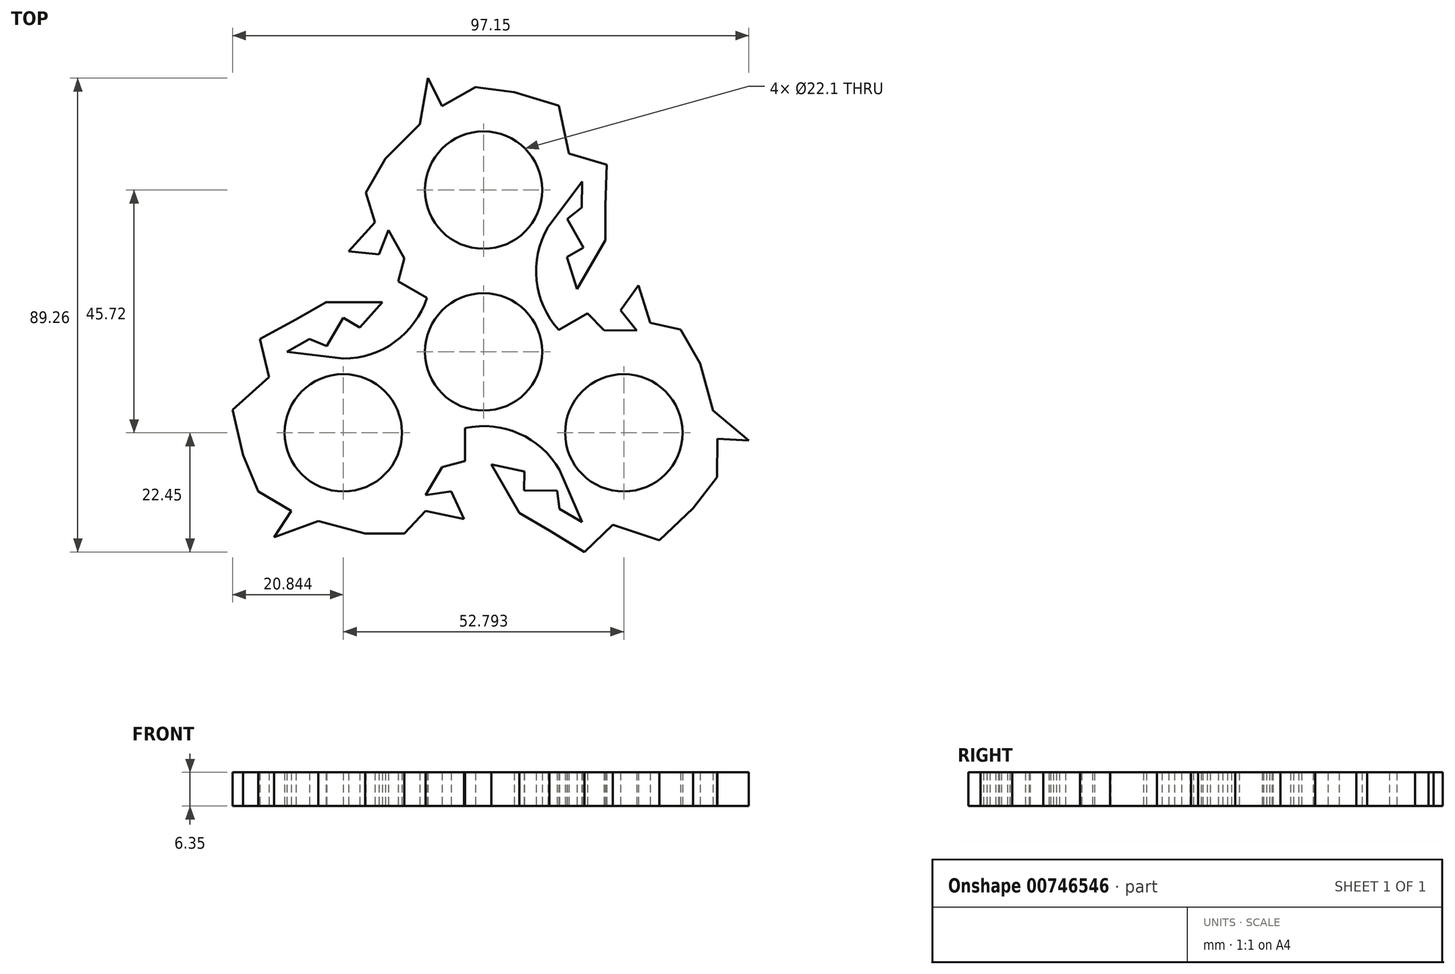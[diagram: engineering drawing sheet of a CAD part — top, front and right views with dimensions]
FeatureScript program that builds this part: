
annotation { "Feature Type Name" : "Feature", "Feature Type Description" : "" }
export const myFeature = defineFeature(function(context is Context, id is Id, definition is map)
    precondition{}
    {
        {
            var Q0;
            Q0=qCreatedBy(makeId("Top.planeOp"),FACE);
            var sketch = newSketch(context, id + "F0", { "sketchPlane" : qUnion([Q0])});
            skCircle(sketch, "E0", {"center": v(0, 0) * mm, "radius": 11.05 * mm});
            skCircle(sketch, "E1", {"center": v(0, 0) * mm, "radius": 13.97 * mm});
            skCircle(sketch, "E2", {"center": v(0, 30.48) * mm, "radius": 11.05 * mm});
            skCircle(sketch, "E3", {"center": v(0, 30.48) * mm, "radius": 13.97 * mm});
            skCircle(sketch, "E4.1.0", {"center": v(-26.4, -15.24) * mm, "radius": 13.97 * mm});
            skCircle(sketch, "E4.1.1", {"center": v(-26.4, -15.24) * mm, "radius": 11.05 * mm});
            skCircle(sketch, "E4.2.0", {"center": v(26.4, -15.24) * mm, "radius": 13.97 * mm});
            skCircle(sketch, "E4.2.1", {"center": v(26.4, -15.24) * mm, "radius": 11.05 * mm});
            skArc(sketch, "E5", {"start": v(-26.4, -1.27) * mm, "mid": v(-12.1, 6.99) * mm, "end": v(-12.1, 23.5) * mm});
            skArc(sketch, "E6.1.0", {"start": v(14.3, -22.22) * mm, "mid": v(0, -13.97) * mm, "end": v(-14.3, -22.23) * mm});
            skArc(sketch, "E6.2.0", {"start": v(12.1, 23.5) * mm, "mid": v(12.1, 6.99) * mm, "end": v(26.4, -1.27) * mm});
            skLineSegment(sketch, "E7", {"start": v(-37.03, 0) * mm, "end": v(-32.77, 2.41) * mm});
            skLineSegment(sketch, "E8", {"start": v(-32.77, 2.41) * mm, "end": v(-29.55, 1.1) * mm});
            skLineSegment(sketch, "E9", {"start": v(-29.55, 1.1) * mm, "end": v(-26.4, 6.44) * mm});
            skLineSegment(sketch, "E10", {"start": v(-26.4, 6.44) * mm, "end": v(-23.32, 4.62) * mm});
            skLineSegment(sketch, "E11", {"start": v(-23.32, 4.62) * mm, "end": v(-19.05, 9.33) * mm});
            skLineSegment(sketch, "E12", {"start": v(-19.05, 9.33) * mm, "end": v(-23.12, 9.33) * mm});
            skLineSegment(sketch, "E13", {"start": v(-23.12, 9.33) * mm, "end": v(-29.65, 9.33) * mm});
            skLineSegment(sketch, "E14", {"start": v(-29.65, 9.33) * mm, "end": v(-35.32, 6.1) * mm});
            skLineSegment(sketch, "E15", {"start": v(-35.32, 6.1) * mm, "end": v(-42.13, 2.41) * mm});
            skLineSegment(sketch, "E16", {"start": v(-42.13, 2.41) * mm, "end": v(-40.37, -4.74) * mm});
            skLineSegment(sketch, "E17", {"start": v(-40.37, -4.74) * mm, "end": v(-47.24, -10.92) * mm});
            skLineSegment(sketch, "E18", {"start": v(-47.24, -10.92) * mm, "end": v(-45.25, -19.44) * mm});
            skLineSegment(sketch, "E19", {"start": v(-45.25, -19.44) * mm, "end": v(-42.42, -26.24) * mm});
            skLineSegment(sketch, "E20", {"start": v(-42.42, -26.24) * mm, "end": v(-36.17, -29.93) * mm});
            skLineSegment(sketch, "E21", {"start": v(-36.17, -29.93) * mm, "end": v(-39.4, -34.88) * mm});
            skLineSegment(sketch, "E22", {"start": v(-39.4, -34.88) * mm, "end": v(-31.15, -31.86) * mm});
            skLineSegment(sketch, "E23", {"start": v(-31.15, -31.86) * mm, "end": v(-22.27, -34.19) * mm});
            skLineSegment(sketch, "E24", {"start": v(-22.27, -34.19) * mm, "end": v(-14.9, -34.19) * mm});
            skLineSegment(sketch, "E25", {"start": v(-14.9, -34.19) * mm, "end": v(-10.92, -29.93) * mm});
            skLineSegment(sketch, "E26", {"start": v(-10.92, -29.93) * mm, "end": v(-3.71, -31.5) * mm});
            skLineSegment(sketch, "E27", {"start": v(-3.71, -31.5) * mm, "end": v(-6.1, -26.24) * mm});
            skLineSegment(sketch, "E28", {"start": v(-6.1, -26.24) * mm, "end": v(-10.92, -26.99) * mm});
            skLineSegment(sketch, "E29", {"start": v(-10.92, -26.99) * mm, "end": v(-7.8, -21.7) * mm});
            skLineSegment(sketch, "E30", {"start": v(-7.8, -21.7) * mm, "end": v(-3.48, -20.55) * mm});
            skLineSegment(sketch, "E31", {"start": v(-3.48, -20.55) * mm, "end": v(-3.48, -13.53) * mm});
            skLineSegment(sketch, "E32", {"start": v(-37.03, 0) * mm, "end": v(-26.4, -1.27) * mm});
            skLineSegment(sketch, "E33.1.0", {"start": v(15.66, 17.88) * mm, "end": v(17.6, 11.83) * mm});
            skLineSegment(sketch, "E33.1.1", {"start": v(17.6, 11.83) * mm, "end": v(19.64, 15.36) * mm});
            skLineSegment(sketch, "E33.1.2", {"start": v(19.64, 15.36) * mm, "end": v(22.9, 21.01) * mm});
            skLineSegment(sketch, "E33.1.3", {"start": v(22.9, 21.01) * mm, "end": v(22.94, 27.54) * mm});
            skLineSegment(sketch, "E33.1.4", {"start": v(22.94, 27.54) * mm, "end": v(23.16, 35.28) * mm});
            skLineSegment(sketch, "E33.1.5", {"start": v(23.16, 35.28) * mm, "end": v(16.08, 37.33) * mm});
            skLineSegment(sketch, "E33.1.6", {"start": v(16.08, 37.33) * mm, "end": v(14.16, 46.37) * mm});
            skLineSegment(sketch, "E33.1.7", {"start": v(14.16, 46.37) * mm, "end": v(5.8, 48.9) * mm});
            skLineSegment(sketch, "E33.1.8", {"start": v(5.8, 48.9) * mm, "end": v(-1.52, 49.86) * mm});
            skLineSegment(sketch, "E33.1.9", {"start": v(-1.52, 49.86) * mm, "end": v(-7.84, 46.3) * mm});
            skLineSegment(sketch, "E33.1.10", {"start": v(-7.84, 46.3) * mm, "end": v(-10.5, 51.57) * mm});
            skLineSegment(sketch, "E33.1.11", {"start": v(-10.5, 51.57) * mm, "end": v(-12.02, 42.9) * mm});
            skLineSegment(sketch, "E33.1.12", {"start": v(-12.02, 42.9) * mm, "end": v(-18.47, 36.38) * mm});
            skLineSegment(sketch, "E33.1.13", {"start": v(-18.47, 36.38) * mm, "end": v(-22.16, 30) * mm});
            skLineSegment(sketch, "E33.1.14", {"start": v(-22.16, 30) * mm, "end": v(-20.46, 24.43) * mm});
            skLineSegment(sketch, "E33.1.15", {"start": v(-20.46, 24.43) * mm, "end": v(-25.43, 18.97) * mm});
            skLineSegment(sketch, "E33.1.16", {"start": v(-17.91, 22.95) * mm, "end": v(-14.9, 17.6) * mm});
            skLineSegment(sketch, "E33.1.17", {"start": v(-14.9, 17.6) * mm, "end": v(-16.06, 13.28) * mm});
            skLineSegment(sketch, "E33.1.18", {"start": v(-16.06, 13.28) * mm, "end": v(-9.98, 9.78) * mm});
            skLineSegment(sketch, "E33.1.19", {"start": v(15.74, 25.04) * mm, "end": v(18.78, 19.64) * mm});
            skLineSegment(sketch, "E33.1.20", {"start": v(18.47, 27.17) * mm, "end": v(15.74, 25.04) * mm});
            skLineSegment(sketch, "E33.1.21", {"start": v(18.51, 32.07) * mm, "end": v(18.47, 27.17) * mm});
            skLineSegment(sketch, "E33.1.22", {"start": v(18.51, 32.07) * mm, "end": v(12.1, 23.5) * mm});
            skLineSegment(sketch, "E33.1.23", {"start": v(-19.68, 18.4) * mm, "end": v(-17.91, 22.95) * mm});
            skLineSegment(sketch, "E33.1.24", {"start": v(-25.43, 18.97) * mm, "end": v(-19.68, 18.4) * mm});
            skLineSegment(sketch, "E33.2.0", {"start": v(7.66, -22.5) * mm, "end": v(1.44, -21.16) * mm});
            skLineSegment(sketch, "E33.2.1", {"start": v(1.44, -21.16) * mm, "end": v(3.48, -24.7) * mm});
            skLineSegment(sketch, "E33.2.2", {"start": v(3.48, -24.7) * mm, "end": v(6.74, -30.34) * mm});
            skLineSegment(sketch, "E33.2.3", {"start": v(6.74, -30.34) * mm, "end": v(12.38, -33.64) * mm});
            skLineSegment(sketch, "E33.2.4", {"start": v(12.38, -33.64) * mm, "end": v(18.98, -37.7) * mm});
            skLineSegment(sketch, "E33.2.5", {"start": v(18.98, -37.7) * mm, "end": v(24.3, -32.59) * mm});
            skLineSegment(sketch, "E33.2.6", {"start": v(24.3, -32.59) * mm, "end": v(33.08, -35.45) * mm});
            skLineSegment(sketch, "E33.2.7", {"start": v(33.08, -35.45) * mm, "end": v(39.46, -29.47) * mm});
            skLineSegment(sketch, "E33.2.8", {"start": v(39.46, -29.47) * mm, "end": v(43.94, -23.61) * mm});
            skLineSegment(sketch, "E33.2.9", {"start": v(43.94, -23.61) * mm, "end": v(44, -16.36) * mm});
            skLineSegment(sketch, "E33.2.10", {"start": v(44, -16.36) * mm, "end": v(49.91, -16.69) * mm});
            skLineSegment(sketch, "E33.2.11", {"start": v(49.91, -16.69) * mm, "end": v(43.16, -11.05) * mm});
            skLineSegment(sketch, "E33.2.12", {"start": v(43.16, -11.05) * mm, "end": v(40.74, -2.2) * mm});
            skLineSegment(sketch, "E33.2.13", {"start": v(40.74, -2.2) * mm, "end": v(37.06, 4.2) * mm});
            skLineSegment(sketch, "E33.2.14", {"start": v(37.06, 4.2) * mm, "end": v(31.38, 5.5) * mm});
            skLineSegment(sketch, "E33.2.15", {"start": v(31.38, 5.5) * mm, "end": v(29.14, 12.54) * mm});
            skLineSegment(sketch, "E33.2.16", {"start": v(28.84, 4.03) * mm, "end": v(22.7, 4.1) * mm});
            skLineSegment(sketch, "E33.2.17", {"start": v(22.7, 4.1) * mm, "end": v(19.53, 7.26) * mm});
            skLineSegment(sketch, "E33.2.18", {"start": v(19.53, 7.26) * mm, "end": v(13.46, 3.75) * mm});
            skLineSegment(sketch, "E33.2.19", {"start": v(13.82, -26.15) * mm, "end": v(7.62, -26.08) * mm});
            skLineSegment(sketch, "E33.2.20", {"start": v(14.3, -29.59) * mm, "end": v(13.82, -26.15) * mm});
            skLineSegment(sketch, "E33.2.21", {"start": v(18.51, -32.07) * mm, "end": v(14.3, -29.59) * mm});
            skLineSegment(sketch, "E33.2.22", {"start": v(18.51, -32.07) * mm, "end": v(14.3, -22.22) * mm});
            skLineSegment(sketch, "E33.2.23", {"start": v(25.77, 7.85) * mm, "end": v(28.84, 4.03) * mm});
            skLineSegment(sketch, "E33.2.24", {"start": v(29.14, 12.54) * mm, "end": v(25.77, 7.85) * mm});
            skLineSegment(sketch, "E33.anchor1", {"start": v(0, 0) * mm, "end": v(-23.32, 4.62) * mm, "construction": true});
            skLineSegment(sketch, "E34", {"start": v(15.66, 17.88) * mm, "end": v(18.78, 19.64) * mm});
            skLineSegment(sketch, "E35", {"start": v(7.62, -26.08) * mm, "end": v(7.66, -22.5) * mm});
            skSolve(sketch);
        }
        {
            var Q0;
            Q0=qSketchRegion(id+"F0",true);
            extrude(context, id + "F1", {"entities" : qUnion([Q0]), "depth" : 6.35 * mm, "offsetDistance" : 25.4 * mm});
        }
    });
